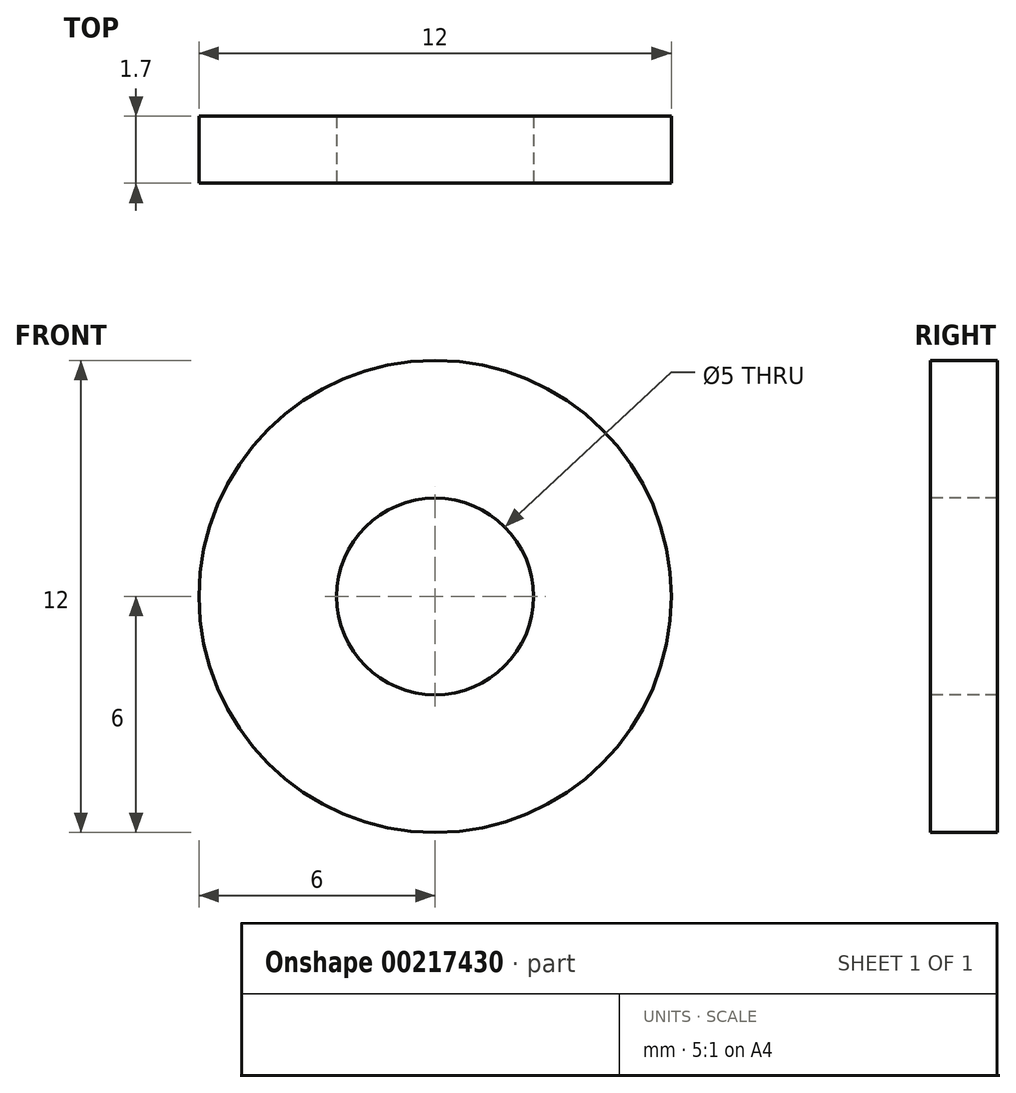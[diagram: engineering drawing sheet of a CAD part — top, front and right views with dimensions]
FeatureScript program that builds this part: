
annotation { "Feature Type Name" : "Feature", "Feature Type Description" : "" }
export const myFeature = defineFeature(function(context is Context, id is Id, definition is map)
    precondition{}
    {
        {
            assignVariable(context, id + "F0", {"name" : "Depth", "anyValue" : 1.7});
        }
        {
            assignVariable(context, id + "F1", {"name" : "Inner_Diameter", "anyValue" : 5});
        }
        {
            assignVariable(context, id + "F2", {"name" : "Di", "anyValue" : getVariable(context, 'Inner_Diameter')});
        }
        {
            var Q0;
            Q0=qCreatedBy(makeId("Front.planeOp"),FACE);
            var sketch = newSketch(context, id + "F3", { "sketchPlane" : qUnion([Q0])});
            skCircle(sketch, "E0", {"center": v(0, 0) * mm, "radius": 6 * mm});
            skSolve(sketch);
        }
        {
            var Q0;
            Q0=makeQuery(id+"F3.imprint","IMPRINT",FACE,{"disambiguationData":[TD([[makeQuery(id+"F3.imprint","IMPRINT",EDGE,{"derivedFrom":sQuery(id+"F3.wireOp",EDGE,"E0")}),1.0]])]});
            var Q1;
            Q1=sQuery(id+"F3.wireOp",EDGE,"E0");
            extrude(context, id + "F4", {"entities" : qUnion([Q0]), "surfaceEntities" : qUnion([Q1]), "depth" : (getVariable(context, 'Depth')) * mm});
        }
        {
            var Q0;
            Q0=makeQuery(id+"F4.opExtrude","CAP_FACE",FACE,{"disambiguationData":[OSD([sQuery(id+"F3.wireOp",EDGE,"E0")])],"isStart":false});
            var sketch = newSketch(context, id + "F5", { "sketchPlane" : qUnion([Q0])});
            skPoint(sketch, "E1", {"position": v(0, 0) * mm});
            skSolve(sketch);
        }
        {
            var Q0;
            Q0=sQuery(id+"F5.wireOp",VERTEX,"E1");
            var Q1;
            Q1=makeQuery(id+"F4.opExtrude","SWEPT_BODY",BODY,{"disambiguationData":[OSD([sQuery(id+"F3.wireOp",EDGE,"E0")])]});
            hole(context, id + "F6", {"style" : HoleStyle.SIMPLE, "endStyle" : HoleEndStyle.THROUGH, "holeDiameter" : (getVariable(context, 'Di')) * mm, "locations" : qUnion([Q0]), "scope" : qUnion([Q1]), "isTappedThrough" : true});
        }
    });
